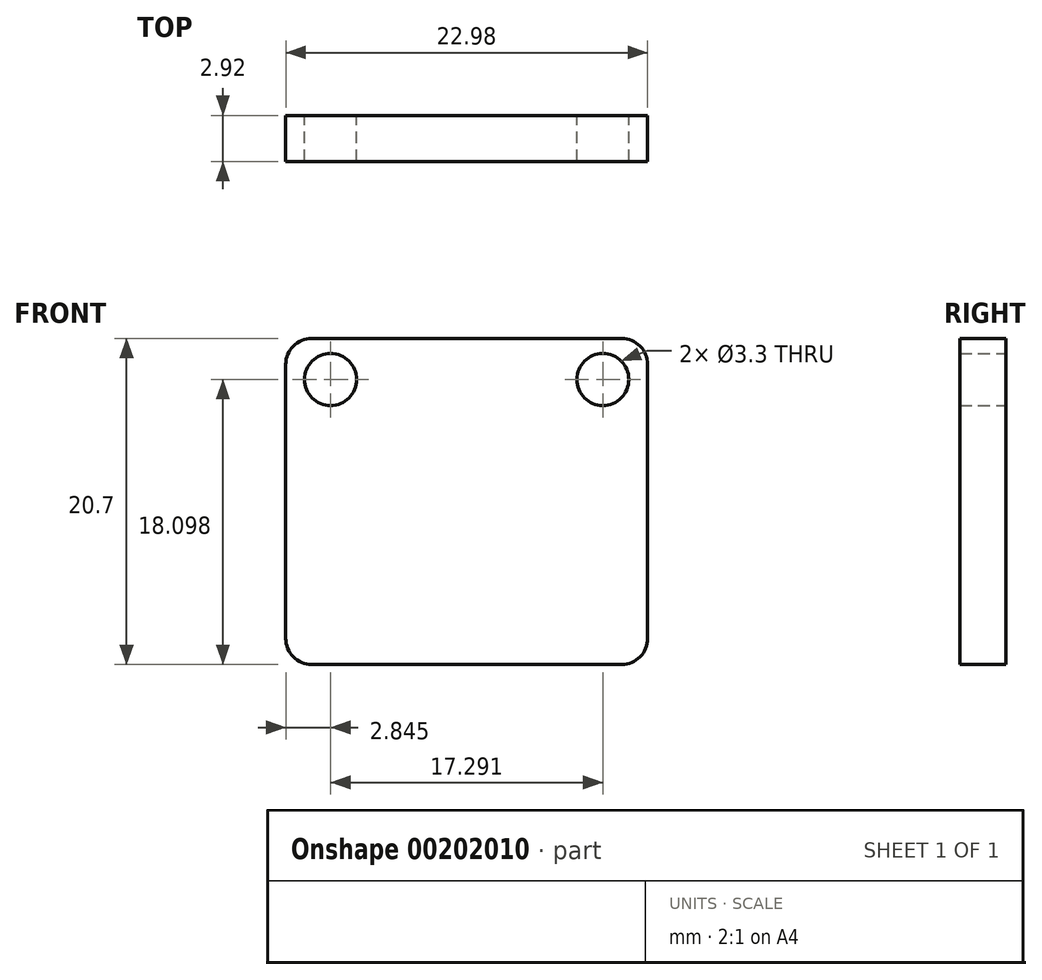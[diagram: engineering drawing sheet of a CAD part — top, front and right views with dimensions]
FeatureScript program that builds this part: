
annotation { "Feature Type Name" : "Feature", "Feature Type Description" : "" }
export const myFeature = defineFeature(function(context is Context, id is Id, definition is map)
    precondition{}
    {
        {
            var Q0;
            Q0=qCreatedBy(makeId("Front.planeOp"),FACE);
            var sketch = newSketch(context, id + "F0", { "sketchPlane" : qUnion([Q0])});
            skLineSegment(sketch, "E0.bottom", {"start": v(-9.84, 10.35) * mm, "end": v(9.84, 10.35) * mm});
            skLineSegment(sketch, "E0.top", {"start": v(-9.84, -10.35) * mm, "end": v(9.84, -10.35) * mm});
            skLineSegment(sketch, "E0.left", {"start": v(-11.5, 8.7) * mm, "end": v(-11.5, -8.7) * mm});
            skLineSegment(sketch, "E0.right", {"start": v(11.5, 8.7) * mm, "end": v(11.5, -8.7) * mm});
            skPoint(sketch, "E0.middle", {"position": v(0, 0) * mm});
            skPoint(sketch, "E1.visualSharp", {"position": v(-11.5, 10.35) * mm});
            skArc(sketch, "E1.filletArc", {"start": v(-9.84, 10.35) * mm, "mid": v(-11, 9.87) * mm, "end": v(-11.5, 8.7) * mm});
            skPoint(sketch, "E2.visualSharp", {"position": v(11.5, 10.35) * mm});
            skArc(sketch, "E2.filletArc", {"start": v(11.5, 8.7) * mm, "mid": v(11, 9.87) * mm, "end": v(9.84, 10.35) * mm});
            skPoint(sketch, "E3.visualSharp", {"position": v(11.5, -10.35) * mm});
            skArc(sketch, "E3.filletArc", {"start": v(9.84, -10.35) * mm, "mid": v(11, -9.87) * mm, "end": v(11.5, -8.7) * mm});
            skPoint(sketch, "E4.visualSharp", {"position": v(-11.5, -10.35) * mm});
            skArc(sketch, "E4.filletArc", {"start": v(-11.5, -8.7) * mm, "mid": v(-11, -9.87) * mm, "end": v(-9.84, -10.35) * mm});
            skLineSegment(sketch, "E5", {"start": v(-11, 9.87) * mm, "end": v(11, -9.87) * mm, "construction": true});
            skLineSegment(sketch, "E6", {"start": v(11, 9.87) * mm, "end": v(-11, -9.87) * mm, "construction": true});
            skCircle(sketch, "E7", {"center": v(8.65, 7.75) * mm, "radius": 1.65 * mm});
            skLineSegment(sketch, "E8", {"start": v(-11.5, 0) * mm, "end": v(11.5, 0) * mm, "construction": true});
            skCircle(sketch, "E9.MirrorC", {"center": v(-8.65, 7.75) * mm, "radius": 1.65 * mm});
            skSolve(sketch);
        }
        {
            var Q0;
            Q0=makeQuery(id+"F0.imprint","IMPRINT",FACE,{"disambiguationData":[TD([[makeQuery(id+"F0.imprint","IMPRINT",EDGE,{"derivedFrom":sQuery(id+"F0.wireOp",EDGE,"E0.bottom")}),-1.0]])]});
            extrude(context, id + "F1", {"entities" : qUnion([Q0]), "depth" : 2.92 * mm});
        }
    });
